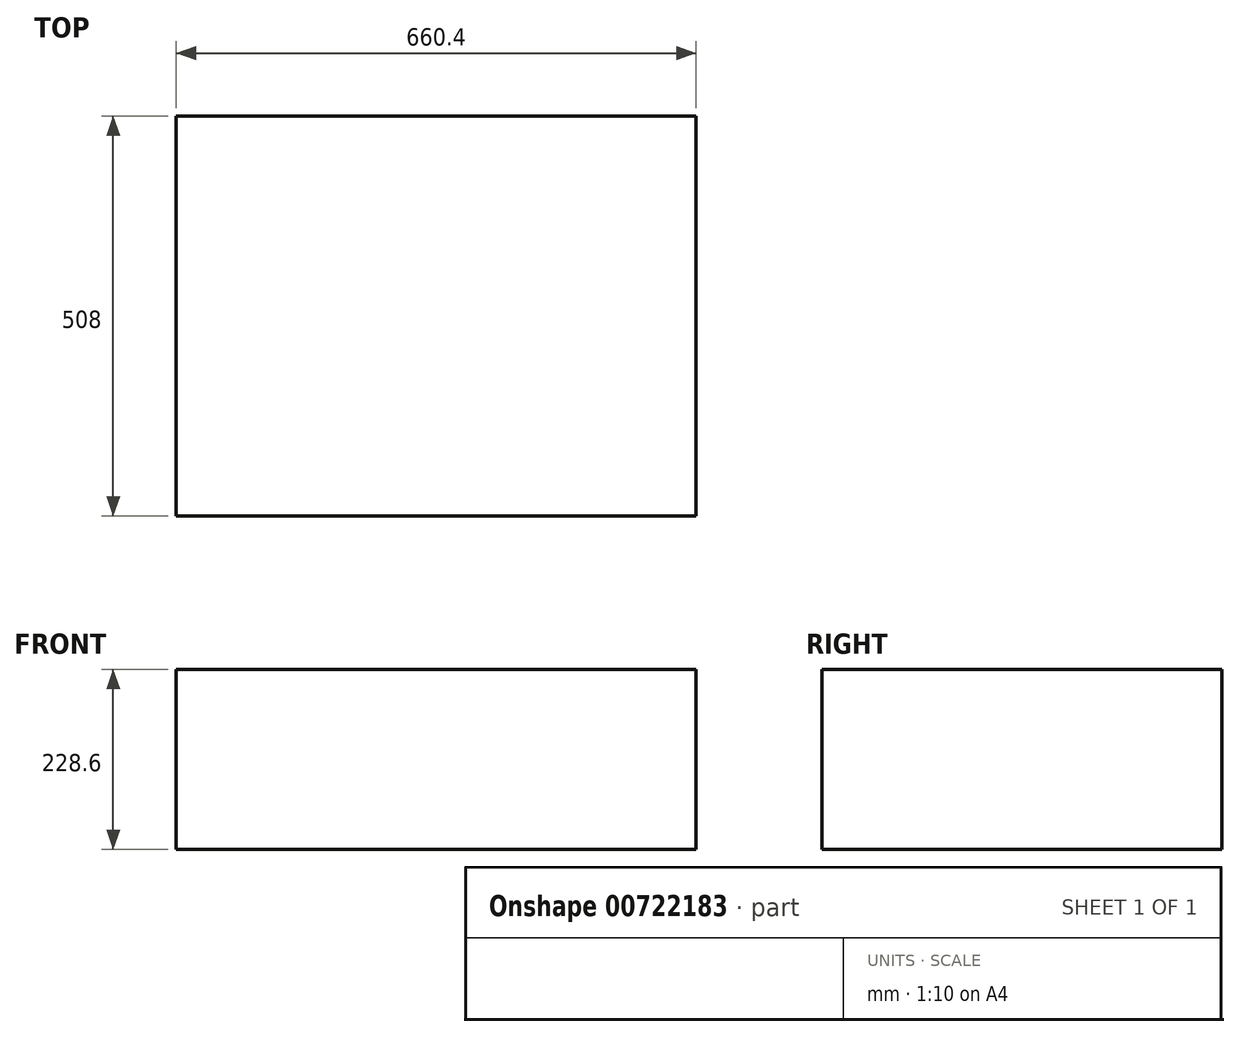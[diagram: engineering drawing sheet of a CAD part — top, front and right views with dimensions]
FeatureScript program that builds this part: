
annotation { "Feature Type Name" : "Feature", "Feature Type Description" : "" }
export const myFeature = defineFeature(function(context is Context, id is Id, definition is map)
    precondition{}
    {
        {
            var Q0;
            Q0=qCreatedBy(makeId("Top.planeOp"),FACE);
            var sketch = newSketch(context, id + "F0", { "sketchPlane" : qUnion([Q0])});
            skLineSegment(sketch, "E0.bottom", {"start": v(-330.2, -254) * mm, "end": v(330.2, -254) * mm});
            skLineSegment(sketch, "E0.top", {"start": v(-330.2, 254) * mm, "end": v(330.2, 254) * mm});
            skLineSegment(sketch, "E0.left", {"start": v(-330.2, -254) * mm, "end": v(-330.2, 254) * mm});
            skLineSegment(sketch, "E0.right", {"start": v(330.2, -254) * mm, "end": v(330.2, 254) * mm});
            skPoint(sketch, "E0.middle", {"position": v(0, 0) * mm});
            skSolve(sketch);
        }
        {
            var Q0;
            Q0 = qSketchRegion(id + "F0", true);
            extrude(context, id + "F1", {"entities" : qUnion([Q0]), "depth" : 228.6 * mm, "offsetDistance" : 25.4 * mm});
        }
    });
